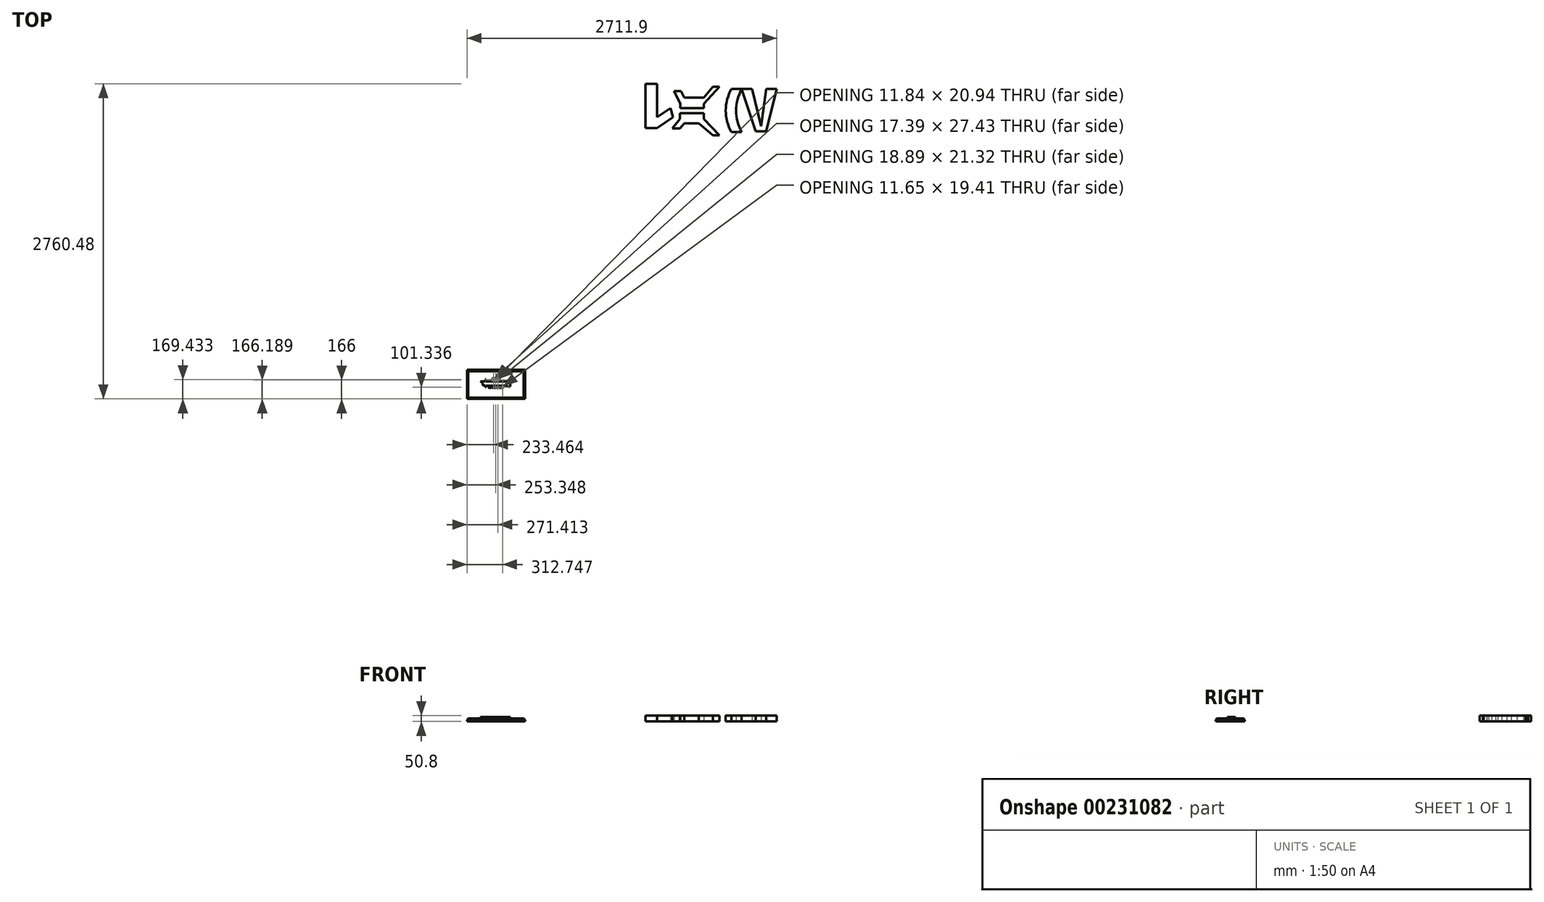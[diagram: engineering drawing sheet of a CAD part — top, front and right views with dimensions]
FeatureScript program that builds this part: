
annotation { "Feature Type Name" : "Feature", "Feature Type Description" : "" }
export const myFeature = defineFeature(function(context is Context, id is Id, definition is map)
    precondition{}
    {
        {
            var Q0;
            Q0=qCreatedBy(makeId("Top.planeOp"),FACE);
            var sketch = newSketch(context, id + "F0", { "sketchPlane" : qUnion([Q0])});
            skLineSegment(sketch, "E0.bottom", {"start": v(457.98, -96.74) * mm, "end": v(666.8, -96.74) * mm});
            skLineSegment(sketch, "E0.top", {"start": v(457.98, -45.22) * mm, "end": v(666.8, -45.22) * mm});
            skLineSegment(sketch, "E0.left", {"start": v(457.98, -96.74) * mm, "end": v(457.98, -45.22) * mm});
            skLineSegment(sketch, "E0.right", {"start": v(666.8, -96.74) * mm, "end": v(666.8, -45.22) * mm});
            skLineSegment(sketch, "E1.bottom", {"start": v(460.92, 0) * mm, "end": v(666.8, 0) * mm});
            skLineSegment(sketch, "E1.top", {"start": v(460.92, 38.4) * mm, "end": v(666.8, 38.4) * mm});
            skLineSegment(sketch, "E1.left", {"start": v(460.92, 0) * mm, "end": v(460.92, 38.4) * mm});
            skLineSegment(sketch, "E1.right", {"start": v(666.8, 0) * mm, "end": v(666.8, 38.4) * mm});
            skLineSegment(sketch, "E2", {"start": v(457.98, -96.74) * mm, "end": v(390.19, -178.1) * mm});
            skLineSegment(sketch, "E3", {"start": v(390.19, -178.1) * mm, "end": v(457.98, -178.1) * mm});
            skLineSegment(sketch, "E4", {"start": v(457.98, -178.1) * mm, "end": v(494.66, -134.09) * mm});
            skLineSegment(sketch, "E5", {"start": v(494.66, -134.09) * mm, "end": v(623.41, -134.09) * mm});
            skLineSegment(sketch, "E6", {"start": v(623.41, -134.09) * mm, "end": v(747.22, -237.26) * mm});
            skLineSegment(sketch, "E7", {"start": v(747.22, -237.26) * mm, "end": v(805.1, -237.26) * mm});
            skLineSegment(sketch, "E8", {"start": v(805.1, -237.26) * mm, "end": v(666.8, -96.74) * mm});
            skLineSegment(sketch, "E9", {"start": v(666.8, 38.4) * mm, "end": v(805.1, 188) * mm});
            skLineSegment(sketch, "E10", {"start": v(805.1, 188) * mm, "end": v(747.22, 188) * mm});
            skLineSegment(sketch, "E11", {"start": v(747.22, 188) * mm, "end": v(666.8, 90.38) * mm});
            skLineSegment(sketch, "E12", {"start": v(666.8, 90.38) * mm, "end": v(494.66, 90.38) * mm});
            skLineSegment(sketch, "E13", {"start": v(494.66, 90.38) * mm, "end": v(466.12, 147.33) * mm});
            skLineSegment(sketch, "E14", {"start": v(466.12, 147.33) * mm, "end": v(406.46, 147.33) * mm});
            skLineSegment(sketch, "E15", {"start": v(406.46, 147.33) * mm, "end": v(460.92, 38.4) * mm});
            skSolve(sketch);
        }
        {
            var Q0;
            Q0=qCreatedBy(makeId("Top.planeOp"),FACE);
            var sketch = newSketch(context, id + "F1", { "sketchPlane" : qUnion([Q0])});
            skLineSegment(sketch, "E16", {"start": v(908.16, -210.64) * mm, "end": v(997.65, -210.64) * mm});
            skLineSegment(sketch, "E17", {"start": v(908.16, -210.64) * mm, "end": v(908.16, 166.31) * mm, "construction": true});
            skArc(sketch, "E18", {"start": v(908.16, 166.31) * mm, "mid": v(859.12, -22.17) * mm, "end": v(908.16, -210.64) * mm});
            skArc(sketch, "E19", {"start": v(997.65, 166.31) * mm, "mid": v(949.8, -22.17) * mm, "end": v(997.65, -210.64) * mm});
            skLineSegment(sketch, "E20", {"start": v(908.16, 166.31) * mm, "end": v(997.65, 166.31) * mm});
            skLineSegment(sketch, "E21", {"start": v(997.65, 166.31) * mm, "end": v(1119.69, -202.5) * mm});
            skLineSegment(sketch, "E22", {"start": v(1119.69, -202.5) * mm, "end": v(1214.6, -202.5) * mm});
            skLineSegment(sketch, "E23", {"start": v(1214.6, -202.5) * mm, "end": v(1304.1, 166.31) * mm});
            skLineSegment(sketch, "E24", {"start": v(1304.1, 166.31) * mm, "end": v(1423.42, -202.5) * mm});
            skLineSegment(sketch, "E25", {"start": v(1423.42, -202.5) * mm, "end": v(1512.92, -202.5) * mm});
            skLineSegment(sketch, "E26", {"start": v(1512.92, -202.5) * mm, "end": v(1396.3, 166.31) * mm});
            skLineSegment(sketch, "E27", {"start": v(1396.3, 166.31) * mm, "end": v(1304.1, 166.31) * mm});
            skLineSegment(sketch, "E28", {"start": v(1304.1, 166.31) * mm, "end": v(1214.6, 166.31) * mm});
            skLineSegment(sketch, "E29", {"start": v(1214.6, 166.31) * mm, "end": v(1168.5, -159.12) * mm});
            skLineSegment(sketch, "E30", {"start": v(1168.5, -159.12) * mm, "end": v(1089.86, 166.31) * mm});
            skLineSegment(sketch, "E31", {"start": v(1089.86, 166.31) * mm, "end": v(997.65, 166.31) * mm});
            skSolve(sketch);
        }
        {
            var Q0;
            Q0=makeQuery(id+"F1.imprint","IMPRINT",FACE,{"disambiguationData":[TD([[makeQuery(id+"F1.imprint","IMPRINT",EDGE,{"derivedFrom":sQuery(id+"F1.wireOp",EDGE,"E21")}),1.0]])]});
            var Q1;
            Q1=makeQuery(id+"F1.imprint","IMPRINT",FACE,{"disambiguationData":[TD([[makeQuery(id+"F1.imprint","IMPRINT",EDGE,{"derivedFrom":sQuery(id+"F1.wireOp",EDGE,"E16")}),1.0]])]});
            var Q2;
            Q2=makeQuery(id+"F0.imprint","IMPRINT",FACE,{"disambiguationData":[TD([[makeQuery(id+"F0.imprint","IMPRINT",EDGE,{"derivedFrom":sQuery(id+"F0.wireOp",EDGE,"E0.bottom")}),1.0]])]});
            var Q3;
            Q3=makeQuery(id+"F0.imprint","IMPRINT",FACE,{"disambiguationData":[TD([[makeQuery(id+"F0.imprint","IMPRINT",EDGE,{"derivedFrom":sQuery(id+"F0.wireOp",EDGE,"E0.bottom")}),-1.0]])]});
            var Q4;
            Q4=makeQuery(id+"F0.imprint","IMPRINT",FACE,{"disambiguationData":[TD([[makeQuery(id+"F0.imprint","IMPRINT",EDGE,{"derivedFrom":sQuery(id+"F0.wireOp",EDGE,"E1.top")}),1.0]])]});
            var Q5;
            Q5=makeQuery(id+"F0.imprint","IMPRINT",FACE,{"disambiguationData":[TD([[makeQuery(id+"F0.imprint","IMPRINT",EDGE,{"derivedFrom":sQuery(id+"F0.wireOp",EDGE,"E1.bottom")}),1.0]])]});
            extrude(context, id + "F2", {"entities" : qUnion([Q0, Q1, Q2, Q3, Q4, Q5]), "depth" : 50.8 * mm});
        }
        {
            var Q0;
            Q0=qCreatedBy(makeId("Top.planeOp"),FACE);
            var sketch = newSketch(context, id + "F3", { "sketchPlane" : qUnion([Q0])});
            skLineSegment(sketch, "E32.bottom", {"start": v(156.96, -175.39) * mm, "end": v(257.3, -175.39) * mm});
            skLineSegment(sketch, "E32.top", {"start": v(156.96, 212.41) * mm, "end": v(257.3, 212.41) * mm});
            skLineSegment(sketch, "E32.left", {"start": v(156.96, -175.39) * mm, "end": v(156.96, 212.41) * mm});
            skLineSegment(sketch, "E32.right", {"start": v(257.3, -175.39) * mm, "end": v(257.3, 212.41) * mm});
            skLineSegment(sketch, "E33", {"start": v(257.3, -175.39) * mm, "end": v(398.32, -80.47) * mm});
            skLineSegment(sketch, "E34", {"start": v(398.32, -80.47) * mm, "end": v(373.92, 0) * mm});
            skLineSegment(sketch, "E35", {"start": v(373.92, 0) * mm, "end": v(257.3, -80.47) * mm});
            skSolve(sketch);
        }
        {
            var Q0;
            {var subQ1=sQuery(id+"F3.wireOp",EDGE,"E32.bottom");Q0=makeQuery(id+"F3.imprint","IMPRINT",FACE,{"disambiguationData":[TD([[makeQuery(id+"F3.imprint","IMPRINT",EDGE,{"derivedFrom":subQ1}),1.0]])]});}
            var Q1;
            {var subQ0=sQuery(id+"F3.wireOp",EDGE,"E33");Q1=makeQuery(id+"F3.imprint","IMPRINT",FACE,{"disambiguationData":[TD([[makeQuery(id+"F3.imprint","IMPRINT",EDGE,{"derivedFrom":subQ0}),1.0]])]});}
            extrude(context, id + "F4", {"entities" : qUnion([Q0, Q1]), "depth" : 50.8 * mm});
        }
        {
            var Q0;
            Q0=qCreatedBy(makeId("Top.planeOp"),FACE);
            var sketch = newSketch(context, id + "F5", { "sketchPlane" : qUnion([Q0])});
            skLineSegment(sketch, "E36.bottom", {"start": v(-1307.88, -2331.94) * mm, "end": v(-1003.08, -2331.94) * mm});
            skLineSegment(sketch, "E36.top", {"start": v(-1307.88, -2478.22) * mm, "end": v(-1003.08, -2478.22) * mm});
            skLineSegment(sketch, "E36.left", {"start": v(-1307.88, -2331.94) * mm, "end": v(-1307.88, -2478.22) * mm});
            skLineSegment(sketch, "E36.right", {"start": v(-1003.08, -2331.94) * mm, "end": v(-1003.08, -2478.22) * mm});
            skLineSegment(sketch, "E37.bottom", {"start": v(-1240.22, -2393.8) * mm, "end": v(-1061.72, -2393.8) * mm});
            skLineSegment(sketch, "E37.top", {"start": v(-1240.22, -2431.18) * mm, "end": v(-1061.72, -2431.18) * mm});
            skLineSegment(sketch, "E37.left", {"start": v(-1240.22, -2393.8) * mm, "end": v(-1240.22, -2431.18) * mm});
            skLineSegment(sketch, "E38.bottom", {"start": v(-1240.22, -2446) * mm, "end": v(-1248.6, -2446) * mm});
            skLineSegment(sketch, "E38.top", {"start": v(-1240.22, -2376.4) * mm, "end": v(-1248.6, -2376.4) * mm});
            skLineSegment(sketch, "E38.left", {"start": v(-1240.22, -2446) * mm, "end": v(-1240.22, -2376.4) * mm});
            skLineSegment(sketch, "E38.right", {"start": v(-1248.6, -2446) * mm, "end": v(-1248.6, -2376.4) * mm});
            skLineSegment(sketch, "E39", {"start": v(-1248.6, -2430.53) * mm, "end": v(-1289.84, -2393.16) * mm});
            skLineSegment(sketch, "E40", {"start": v(-1289.84, -2393.16) * mm, "end": v(-1240.22, -2393.8) * mm});
            skArc(sketch, "E41", {"start": v(-1061.72, -2431.18) * mm, "mid": v(-1046.53, -2440.3) * mm, "end": v(-1028.87, -2438.71) * mm});
            skPoint(sketch, "E42.oppositeSnap0", {"position": v(-1269.22, -2411.84) * mm});
            skLineSegment(sketch, "E42.bottom", {"start": v(-1248.6, -2430.53) * mm, "end": v(-1269.22, -2430.53) * mm});
            skLineSegment(sketch, "E42.top", {"start": v(-1248.6, -2406.78) * mm, "end": v(-1269.22, -2406.78) * mm});
            skLineSegment(sketch, "E42.left", {"start": v(-1248.6, -2430.53) * mm, "end": v(-1248.6, -2406.78) * mm});
            skLineSegment(sketch, "E42.right", {"start": v(-1269.22, -2430.53) * mm, "end": v(-1269.22, -2406.78) * mm});
            skLineSegment(sketch, "E43", {"start": v(-1028.87, -2386.27) * mm, "end": v(-1028.87, -2438.71) * mm});
            skArc(sketch, "E44.trimOffspring", {"start": v(-1028.87, -2386.27) * mm, "mid": v(-1046.53, -2384.67) * mm, "end": v(-1061.72, -2393.8) * mm});
            skLineSegment(sketch, "E45.right", {"start": v(-1028.87, -2393.8) * mm, "end": v(-1028.87, -2396.06) * mm});
            skLineSegment(sketch, "E46.right", {"start": v(-1028.87, -2404) * mm, "end": v(-1028.87, -2406.44) * mm});
            skLineSegment(sketch, "E47.right", {"start": v(-1028.87, -2412.49) * mm, "end": v(-1028.87, -2414.78) * mm});
            skLineSegment(sketch, "E48.bottom", {"start": v(-1066.06, -2393.8) * mm, "end": v(-1061.72, -2393.8) * mm});
            skLineSegment(sketch, "E48.top", {"start": v(-1066.06, -2431.18) * mm, "end": v(-1061.72, -2431.18) * mm});
            skPoint(sketch, "E49.trimOffspring.start.orphan", {"position": v(-1061.72, -2412.49) * mm});
            skSolve(sketch);
        }
        {
            var Q0;
            {var subQ0=sQuery(id+"F5.wireOp",EDGE,"E37.bottom");Q0=makeQuery(id+"F5.imprint","IMPRINT",FACE,{"disambiguationData":[TD([[makeQuery(id+"F5.imprint","IMPRINT",EDGE,{"derivedFrom":subQ0}),-1.0]])]});}
            var Q1;
            Q1=makeQuery(id+"F5.imprint","IMPRINT",FACE,{"disambiguationData":[TD([[makeQuery(id+"F5.imprint","IMPRINT",EDGE,{"derivedFrom":sQuery(id+"F5.wireOp",EDGE,"E37.right")}),1.0]])]});
            var Q2;
            {var subQ0=sQuery(id+"F5.wireOp",EDGE,"E39");Q2=makeQuery(id+"F5.imprint","IMPRINT",FACE,{"disambiguationData":[TD([[makeQuery(id+"F5.imprint","IMPRINT",EDGE,{"derivedFrom":subQ0}),-1.0]])]});}
            var Q3;
            {var subQ1=sQuery(id+"F5.wireOp",EDGE,"E38.bottom");Q3=makeQuery(id+"F5.imprint","IMPRINT",FACE,{"disambiguationData":[TD([[makeQuery(id+"F5.imprint","IMPRINT",EDGE,{"derivedFrom":subQ1}),-1.0]])]});}
            var Q4;
            {var subQ0=sQuery(id+"F5.wireOp",EDGE,"E38.top");Q4=makeQuery(id+"F5.imprint","IMPRINT",FACE,{"disambiguationData":[TD([[makeQuery(id+"F5.imprint","IMPRINT",EDGE,{"derivedFrom":subQ0}),1.0]])]});}
            var Q5;
            {var subQ0=sQuery(id+"F5.wireOp",EDGE,"E42.top");Q5=makeQuery(id+"F5.imprint","IMPRINT",FACE,{"disambiguationData":[TD([[makeQuery(id+"F5.imprint","IMPRINT",EDGE,{"derivedFrom":subQ0}),-1.0]])]});}
            var Q6;
            {var subQ0=sQuery(id+"F5.wireOp",EDGE,"E42.bottom");Q6=makeQuery(id+"F5.imprint","IMPRINT",FACE,{"disambiguationData":[TD([[makeQuery(id+"F5.imprint","IMPRINT",EDGE,{"derivedFrom":subQ0}),-1.0]])]});}
            extrude(context, id + "F6", {"entities" : qUnion([Q0, Q1, Q2, Q3, Q4, Q5, Q6]), "depth" : 38.1 * mm});
        }
        {
            var Q0;
            Q0=qCreatedBy(makeId("Top.planeOp"),FACE);
            var sketch = newSketch(context, id + "F7", { "sketchPlane" : qUnion([Q0])});
            skLineSegment(sketch, "E50.bottom", {"start": v(-1407.8, -2294.07) * mm, "end": v(-899.8, -2294.07) * mm});
            skLineSegment(sketch, "E50.top", {"start": v(-1407.8, -2548.07) * mm, "end": v(-899.8, -2548.07) * mm});
            skLineSegment(sketch, "E50.left", {"start": v(-1407.8, -2294.07) * mm, "end": v(-1407.8, -2548.07) * mm});
            skLineSegment(sketch, "E50.right", {"start": v(-899.8, -2294.07) * mm, "end": v(-899.8, -2548.07) * mm});
            skSolve(sketch);
        }
        {
            var Q0;
            Q0=makeQuery(id+"F7.imprint","IMPRINT",FACE,{"disambiguationData":[TD([[makeQuery(id+"F7.imprint","IMPRINT",EDGE,{"derivedFrom":sQuery(id+"F7.wireOp",EDGE,"E50.bottom")}),-1.0]])]});
            extrude(context, id + "F8", {"entities" : qUnion([Q0]), "operationType" : NewBodyOperationType.ADD, "depth" : 25.4 * mm});
        }
        {
            var Q0;
            Q0=makeQuery(id+"F8.opExtrude","CAP_FACE",FACE,{"disambiguationData":[OSD([sQuery(id+"F7.wireOp",EDGE,"E50.bottom"),sQuery(id+"F7.wireOp",EDGE,"E50.top"),sQuery(id+"F7.wireOp",EDGE,"E50.left"),sQuery(id+"F7.wireOp",EDGE,"E50.right")])],"isStart":false});
            var sketch = newSketch(context, id + "F9", { "sketchPlane" : qUnion([Q0])});
            skText(sketch, "E51", { "text": "Pro\n", "fontName": "OpenSans-Regular.ttf"});
            const initialGuessF9  = {"E51": [-1.1868, -2.39235, 1, 0, 0.02766]};
            skSetInitialGuess(sketch, initialGuessF9);
            skSolve(sketch);
        }
        {
            var Q0;
            Q0=makeQuery(id+"F9.imprint","IMPRINT",FACE,{"disambiguationData":[TD([[makeQuery(id+"F9.imprint","IMPRINT",EDGE,{"derivedFrom":sQuery(id+"F9.wireOp",EDGE,"E51.sketch_text.stroke-0")}),1.0]])]});
            var sketch = newSketch(context, id + "F10", { "sketchPlane" : qUnion([Q0])});
            skText(sketch, "E52", { "text": "Saber shop", "fontName": "OpenSans-Regular.ttf"});
            const initialGuessF10  = {"E52": [-1.21776, -2.4505, 1, 0, 0.0178]};
            skSetInitialGuess(sketch, initialGuessF10);
            skSolve(sketch);
        }
        {
            var Q0;
            Q0 = qSketchRegion(id + "F10", true);
            var Q1;
            Q1 = qSketchRegion(id + "F9", true);
            extrude(context, id + "F11", {"entities" : qUnion([Q0, Q1]), "operationType" : NewBodyOperationType.REMOVE, "oppositeDirection" : true, "depth" : 25.4 * mm});
        }
        {
            var Q0;
            Q0=makeQuery(id+"F8.opExtrude","CAP_EDGE",EDGE,{"disambiguationData":[OSD([sQuery(id+"F7.wireOp",EDGE,"E50.bottom")])],"isStart":false});
            var Q1;
            Q1=makeQuery(id+"F8.opExtrude","CAP_EDGE",EDGE,{"disambiguationData":[OSD([sQuery(id+"F7.wireOp",EDGE,"E50.right")])],"isStart":false});
            var Q2;
            Q2=makeQuery(id+"F8.opExtrude","CAP_EDGE",EDGE,{"disambiguationData":[OSD([sQuery(id+"F7.wireOp",EDGE,"E50.left")])],"isStart":false});
            var Q3;
            Q3=makeQuery(id+"F8.opExtrude","CAP_EDGE",EDGE,{"disambiguationData":[OSD([sQuery(id+"F7.wireOp",EDGE,"E50.top")])],"isStart":false});
            chamfer(context, id + "F12", {"entities" : qUnion([Q0, Q1, Q2, Q3]), "width" : 10.16 * mm, "tangentPropagation" : true});
        }
    });
